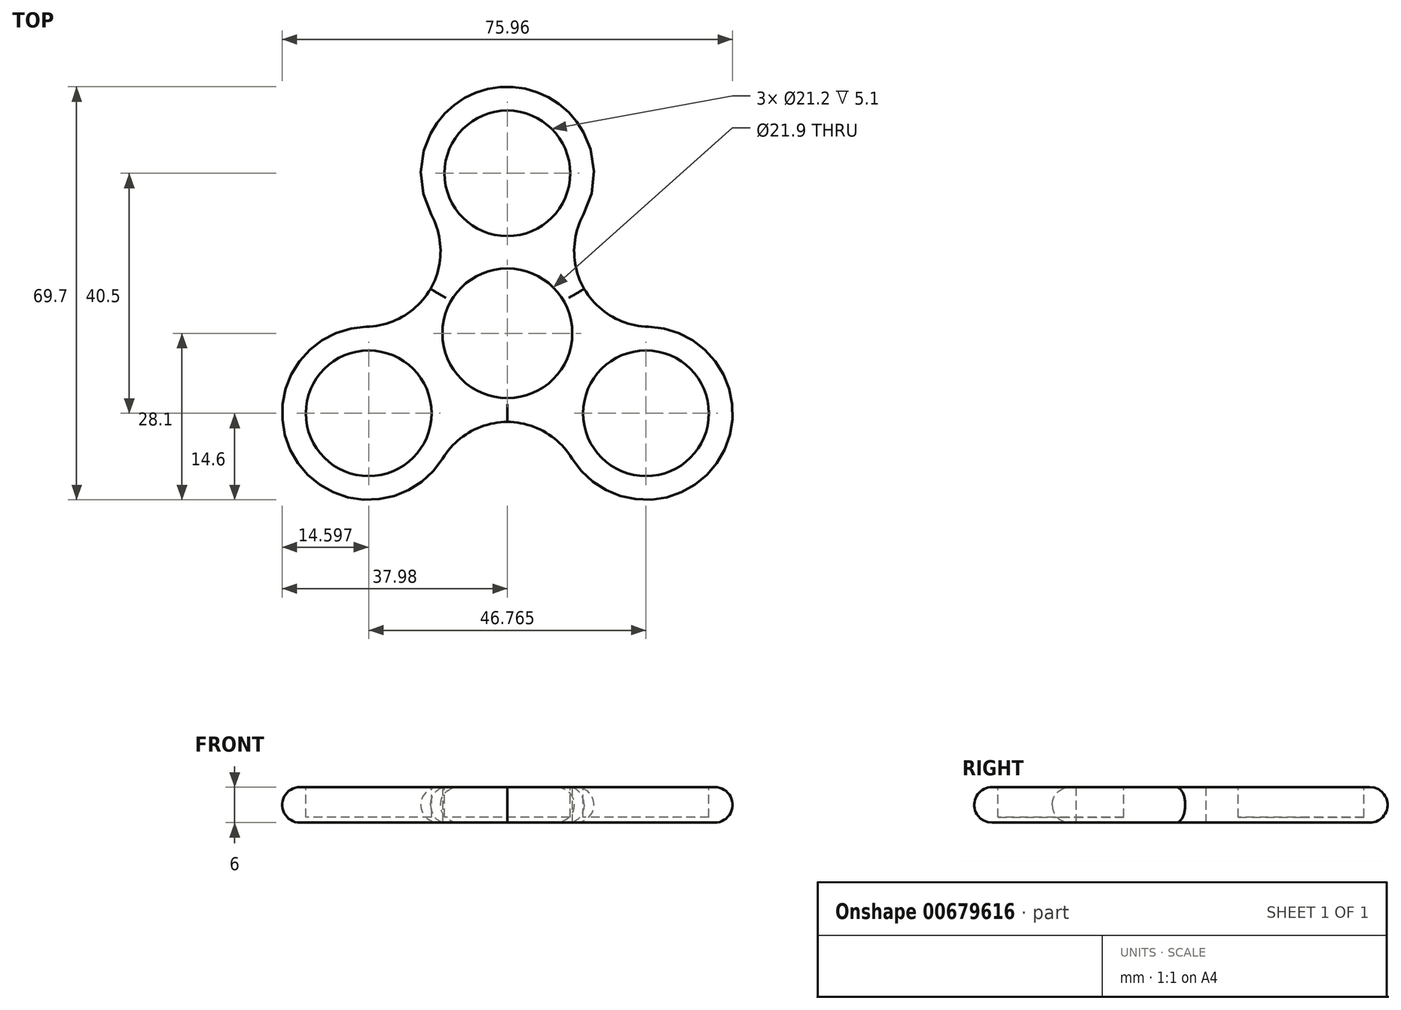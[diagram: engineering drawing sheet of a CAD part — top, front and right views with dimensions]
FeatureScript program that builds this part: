
annotation { "Feature Type Name" : "Feature", "Feature Type Description" : "" }
export const myFeature = defineFeature(function(context is Context, id is Id, definition is map)
    precondition{}
    {
        {
            var Q0;
            Q0=qCreatedBy(makeId("Top.planeOp"),FACE);
            var sketch = newSketch(context, id + "F0", { "sketchPlane" : qUnion([Q0])});
            skCircle(sketch, "E0", {"center": v(0, 0) * mm, "radius": 10.95 * mm});
            skCircle(sketch, "E1.cCircle", {"center": v(0, 0) * mm, "radius": 13.5 * mm, "construction": true});
            skLineSegment(sketch, "E1.0", {"start": v(-23.38, -13.5) * mm, "end": v(0, 27) * mm, "construction": true});
            skLineSegment(sketch, "E1.1", {"start": v(0, 27) * mm, "end": v(23.38, -13.5) * mm, "construction": true});
            skLineSegment(sketch, "E1.2", {"start": v(23.38, -13.5) * mm, "end": v(-23.38, -13.5) * mm, "construction": true});
            skPoint(sketch, "E1.0.midPoint", {"position": v(-11.7, 6.75) * mm});
            skCircle(sketch, "E2", {"center": v(0, 27) * mm, "radius": 10.6 * mm});
            skCircle(sketch, "E3", {"center": v(23.38, -13.5) * mm, "radius": 10.6 * mm});
            skCircle(sketch, "E4", {"center": v(-23.38, -13.5) * mm, "radius": 10.6 * mm});
            skCircle(sketch, "E5.0", {"center": v(-23.38, -13.5) * mm, "radius": 14.6 * mm});
            skCircle(sketch, "E6.0", {"center": v(23.38, -13.5) * mm, "radius": 14.6 * mm});
            skCircle(sketch, "E7.0", {"center": v(0, 27) * mm, "radius": 14.6 * mm});
            skCircle(sketch, "E8.0", {"center": v(0, 0) * mm, "radius": 14.95 * mm});
            skSolve(sketch);
        }
        {
            var Q0;
            Q0=qSketchRegion(id+"F0",true);
            var Q1;
            Q1=makeQuery(id+"F0.imprint","IMPRINT",FACE,{"disambiguationData":[TD([[makeQuery(id+"F0.imprint","IMPRINT",EDGE,{"derivedFrom":sQuery(id+"F0.wireOp",EDGE,"E4")}),1.0]])]});
            var Q2;
            Q2=makeQuery(id+"F0.imprint","IMPRINT",FACE,{"disambiguationData":[TD([[makeQuery(id+"F0.imprint","IMPRINT",EDGE,{"derivedFrom":sQuery(id+"F0.wireOp",EDGE,"E2")}),1.0]])]});
            var Q3;
            Q3=makeQuery(id+"F0.imprint","IMPRINT",FACE,{"disambiguationData":[TD([[makeQuery(id+"F0.imprint","IMPRINT",EDGE,{"derivedFrom":sQuery(id+"F0.wireOp",EDGE,"E3")}),1.0]])]});
            extrude(context, id + "F1", {"entities" : qUnion([Q0, Q1, Q2, Q3]), "depth" : 6 * mm, "offsetDistance" : 25 * mm});
        }
        {
            var Q0;
            {var subQ0=sQuery(id+"F0.wireOp",EDGE,"E8.0");var subQ1=sQuery(id+"F0.wireOp",EDGE,"E5.0");Q0=makeQuery(id+"F1.opExtrude","SWEPT_EDGE",EDGE,{"disambiguationData":[OSD([subQ1,subQ0]),TDD([makeQuery(id+"F0.imprint","INTERSECT",VERTEX,{"disambiguationData":[OD(1.0)],"derivedFrom":[subQ1,subQ0]})])]});}
            var Q1;
            {var subQ0=sQuery(id+"F0.wireOp",EDGE,"E8.0");var subQ1=sQuery(id+"F0.wireOp",EDGE,"E6.0");Q1=makeQuery(id+"F1.opExtrude","SWEPT_EDGE",EDGE,{"disambiguationData":[OSD([subQ1,subQ0]),TDD([makeQuery(id+"F0.imprint","INTERSECT",VERTEX,{"disambiguationData":[OD(0.0)],"derivedFrom":[subQ1,subQ0]})])]});}
            var Q2;
            {var subQ0=sQuery(id+"F0.wireOp",EDGE,"E8.0");var subQ1=sQuery(id+"F0.wireOp",EDGE,"E7.0");Q2=makeQuery(id+"F1.opExtrude","SWEPT_EDGE",EDGE,{"disambiguationData":[OSD([subQ1,subQ0]),TDD([makeQuery(id+"F0.imprint","INTERSECT",VERTEX,{"disambiguationData":[OD(1.0)],"derivedFrom":[subQ1,subQ0]})])]});}
            var Q3;
            {var subQ0=sQuery(id+"F0.wireOp",EDGE,"E8.0");var subQ1=sQuery(id+"F0.wireOp",EDGE,"E6.0");Q3=makeQuery(id+"F1.opExtrude","SWEPT_EDGE",EDGE,{"disambiguationData":[OSD([subQ1,subQ0]),TDD([makeQuery(id+"F0.imprint","INTERSECT",VERTEX,{"disambiguationData":[OD(1.0)],"derivedFrom":[subQ1,subQ0]})])]});}
            var Q4;
            {var subQ0=sQuery(id+"F0.wireOp",EDGE,"E8.0");var subQ1=sQuery(id+"F0.wireOp",EDGE,"E7.0");Q4=makeQuery(id+"F1.opExtrude","SWEPT_EDGE",EDGE,{"disambiguationData":[OSD([subQ1,subQ0]),TDD([makeQuery(id+"F0.imprint","INTERSECT",VERTEX,{"disambiguationData":[OD(0.0)],"derivedFrom":[subQ1,subQ0]})])]});}
            var Q5;
            {var subQ0=sQuery(id+"F0.wireOp",EDGE,"E8.0");var subQ1=sQuery(id+"F0.wireOp",EDGE,"E5.0");Q5=makeQuery(id+"F1.opExtrude","SWEPT_EDGE",EDGE,{"disambiguationData":[OSD([subQ1,subQ0]),TDD([makeQuery(id+"F0.imprint","INTERSECT",VERTEX,{"disambiguationData":[OD(0.0)],"derivedFrom":[subQ1,subQ0]})])]});}
            fillet(context, id + "F2", {"entities" : qUnion([Q0, Q1, Q2, Q3, Q4, Q5]), "radius" : 13 * mm, "tangentPropagation" : true, "allowEdgeOverflow" : false});
        }
        {
            var Q0;
            Q0=makeQuery(id+"F1.opExtrude","CAP_EDGE",EDGE,{"disambiguationData":[OSD([sQuery(id+"F0.wireOp",EDGE,"E7.0")])],"isStart":false});
            var Q1;
            Q1=makeQuery(id+"F1.opExtrude","CAP_EDGE",EDGE,{"disambiguationData":[OSD([sQuery(id+"F0.wireOp",EDGE,"E7.0")])],"isStart":true});
            var Q2;
            Q2=makeQuery(id+"F1.opExtrude","CAP_EDGE",EDGE,{"disambiguationData":[OSD([sQuery(id+"F0.wireOp",EDGE,"E5.0")])],"isStart":false});
            var Q3;
            Q3=makeQuery(id+"F1.opExtrude","CAP_EDGE",EDGE,{"disambiguationData":[OSD([sQuery(id+"F0.wireOp",EDGE,"E5.0")])],"isStart":true});
            var Q4;
            Q4=makeQuery(id+"F1.opExtrude","CAP_EDGE",EDGE,{"disambiguationData":[OSD([sQuery(id+"F0.wireOp",EDGE,"E6.0")])],"isStart":false});
            var Q5;
            Q5=makeQuery(id+"F1.opExtrude","CAP_EDGE",EDGE,{"disambiguationData":[OSD([sQuery(id+"F0.wireOp",EDGE,"E6.0")])],"isStart":true});
            fillet(context, id + "F3", {"entities" : qUnion([Q0, Q1, Q2, Q3, Q4, Q5]), "radius" : 3 * mm, "tangentPropagation" : true, "allowEdgeOverflow" : false});
        }
        {
            var Q0;
            Q0=makeQuery(id+"F1.opExtrude","CAP_FACE",FACE,{"disambiguationData":[OSD([sQuery(id+"F0.wireOp",EDGE,"E0"),sQuery(id+"F0.wireOp",EDGE,"E5.0"),sQuery(id+"F0.wireOp",EDGE,"E6.0"),sQuery(id+"F0.wireOp",EDGE,"E7.0"),sQuery(id+"F0.wireOp",EDGE,"E8.0")])],"isStart":false});
            var sketch = newSketch(context, id + "F4", { "sketchPlane" : qUnion([Q0])});
            skCircle(sketch, "E9", {"center": v(0, 27) * mm, "radius": 10.6 * mm});
            skCircle(sketch, "E10", {"center": v(-23.38, -13.5) * mm, "radius": 10.6 * mm});
            skCircle(sketch, "E11", {"center": v(23.38, -13.5) * mm, "radius": 10.6 * mm});
            skSolve(sketch);
        }
        {
            var Q0;
            Q0=qSketchRegion(id+"F4",true);
            extrude(context, id + "F5", {"entities" : qUnion([Q0]), "operationType" : NewBodyOperationType.REMOVE, "oppositeDirection" : true, "depth" : 5.1 * mm, "offsetDistance" : 25 * mm});
        }
    });
